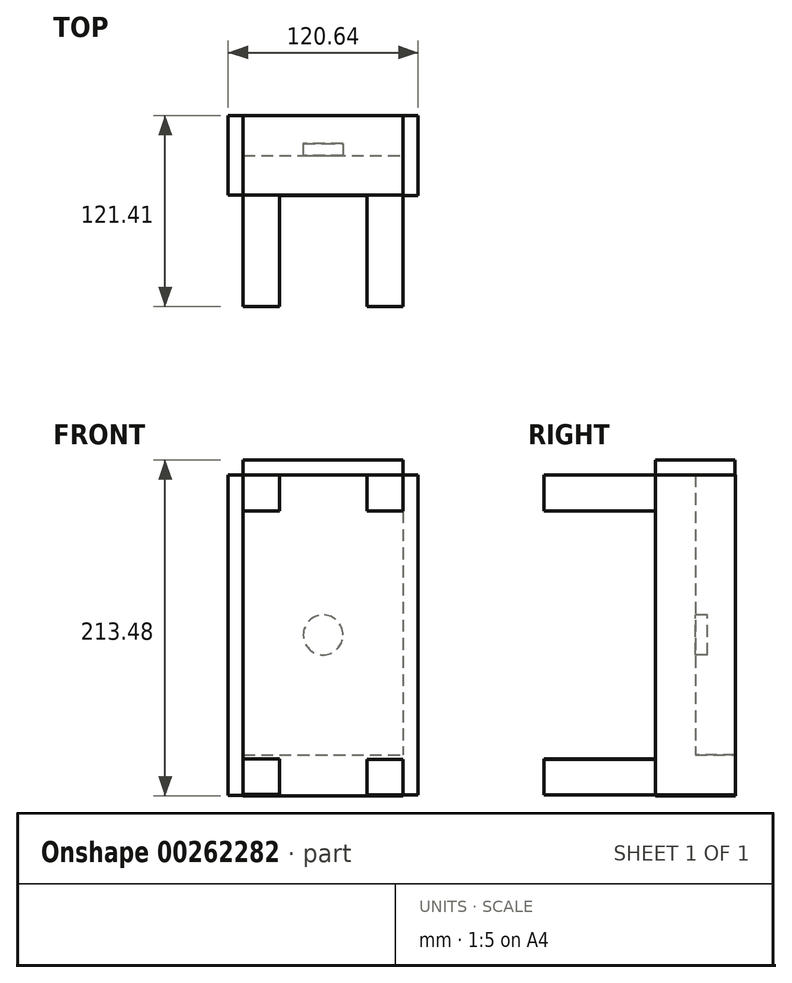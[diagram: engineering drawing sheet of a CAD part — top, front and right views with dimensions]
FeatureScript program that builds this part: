
annotation { "Feature Type Name" : "Feature", "Feature Type Description" : "" }
export const myFeature = defineFeature(function(context is Context, id is Id, definition is map)
    precondition{}
    {
        {
            var Q0;
            Q0=qCreatedBy(makeId("Front.planeOp"),FACE);
            var sketch = newSketch(context, id + "F0", { "sketchPlane" : qUnion([Q0])});
            skLineSegment(sketch, "E0.bottom", {"start": v(-50.8, 101.6) * mm, "end": v(50.8, 101.6) * mm});
            skLineSegment(sketch, "E0.top", {"start": v(-50.8, -101.6) * mm, "end": v(50.8, -101.6) * mm});
            skLineSegment(sketch, "E0.left", {"start": v(-50.8, 101.6) * mm, "end": v(-50.8, -101.6) * mm});
            skLineSegment(sketch, "E0.right", {"start": v(50.8, 101.6) * mm, "end": v(50.8, -101.6) * mm});
            skPoint(sketch, "E0.middle", {"position": v(0, 0) * mm});
            skSolve(sketch);
        }
        {
            var Q0;
            Q0 = qSketchRegion(id + "F0", true);
            extrude(context, id + "F1", {"entities" : qUnion([Q0]), "depth" : 25.4 * mm});
        }
        {
            var Q0;
            Q0=makeQuery(id+"F1.opExtrude","CAP_FACE",FACE,{"disambiguationData":[OSD([sQuery(id+"F0.wireOp",EDGE,"E0.bottom"),sQuery(id+"F0.wireOp",EDGE,"E0.top"),sQuery(id+"F0.wireOp",EDGE,"E0.left"),sQuery(id+"F0.wireOp",EDGE,"E0.right")])],"isStart":false});
            var sketch = newSketch(context, id + "F2", { "sketchPlane" : qUnion([Q0])});
            skPoint(sketch, "E1.middle", {"position": v(0, 54.08) * mm});
            skPoint(sketch, "E2.right.start.orphan", {"position": v(-17.2, 66.12) * mm});
            skPoint(sketch, "E3.bottom.start.orphan", {"position": v(17.2, 66.12) * mm});
            skPoint(sketch, "E3.right.start.orphan", {"position": v(41.3, 66.12) * mm});
            skLineSegment(sketch, "E4.bottom", {"start": v(50.8, 101.6) * mm, "end": v(27.86, 101.6) * mm});
            skLineSegment(sketch, "E4.top", {"start": v(50.8, 78.82) * mm, "end": v(27.86, 78.82) * mm});
            skLineSegment(sketch, "E4.left", {"start": v(50.8, 101.6) * mm, "end": v(50.8, 78.82) * mm});
            skLineSegment(sketch, "E4.right", {"start": v(27.86, 101.6) * mm, "end": v(27.86, 78.82) * mm});
            skPoint(sketch, "E4.middle", {"position": v(39.33, 90.21) * mm});
            skLineSegment(sketch, "E5.left", {"start": v(-35.15, 90.21) * mm, "end": v(-35.15, 90.21) * mm});
            skLineSegment(sketch, "E5.right", {"start": v(113.8, 90.21) * mm, "end": v(113.8, 90.21) * mm});
            skLineSegment(sketch, "E6.bottom", {"start": v(-50.8, 101.6) * mm, "end": v(-27.86, 101.6) * mm});
            skLineSegment(sketch, "E6.left", {"start": v(-50.8, 101.6) * mm, "end": v(-50.8, 78.82) * mm});
            skLineSegment(sketch, "E6.right", {"start": v(-27.86, 101.6) * mm, "end": v(-27.86, 78.82) * mm});
            skPoint(sketch, "E6.middle", {"position": v(-39.33, 90.21) * mm});
            skLineSegment(sketch, "E7.bottom", {"start": v(-39.33, -89.96) * mm, "end": v(-39.33, -89.96) * mm});
            skLineSegment(sketch, "E7.top", {"start": v(-39.33, -94.87) * mm, "end": v(-39.33, -94.87) * mm});
            skLineSegment(sketch, "E7.left", {"start": v(-39.33, -92.41) * mm, "end": v(-39.33, -94.87) * mm});
            skLineSegment(sketch, "E7.right", {"start": v(-39.33, -92.41) * mm, "end": v(-39.33, -94.87) * mm});
            skPoint(sketch, "E7.middle", {"position": v(-39.33, -92.41) * mm});
            skLineSegment(sketch, "E8.bottom", {"start": v(-50.8, -78.64) * mm, "end": v(-27.86, -78.64) * mm});
            skLineSegment(sketch, "E8.top", {"start": v(-50.8, -101.27) * mm, "end": v(-27.86, -101.27) * mm});
            skLineSegment(sketch, "E8.left", {"start": v(-50.8, -78.64) * mm, "end": v(-50.8, -101.27) * mm});
            skLineSegment(sketch, "E8.right", {"start": v(-27.86, -78.64) * mm, "end": v(-27.86, -101.27) * mm});
            skPoint(sketch, "E8.middle", {"position": v(-39.33, -89.96) * mm});
            skLineSegment(sketch, "E9.left", {"start": v(39.33, -92.41) * mm, "end": v(39.33, -92.41) * mm});
            skLineSegment(sketch, "E9.right", {"start": v(-118, -92.41) * mm, "end": v(-118, -92.41) * mm});
            skLineSegment(sketch, "E10.bottom", {"start": v(50.8, -78.89) * mm, "end": v(27.86, -78.89) * mm});
            skLineSegment(sketch, "E10.top", {"start": v(50.8, -101.52) * mm, "end": v(27.86, -101.52) * mm});
            skLineSegment(sketch, "E10.left", {"start": v(50.8, -78.89) * mm, "end": v(50.8, -101.52) * mm});
            skLineSegment(sketch, "E10.right", {"start": v(27.86, -78.89) * mm, "end": v(27.86, -101.52) * mm});
            skPoint(sketch, "E10.middle", {"position": v(39.33, -90.2) * mm});
            skLineSegment(sketch, "E11", {"start": v(-50.8, 78.82) * mm, "end": v(-27.86, 78.82) * mm});
            skSolve(sketch);
        }
        {
            var Q0;
            Q0 = qSketchRegion(id + "F2", true);
            extrude(context, id + "F3", {"entities" : qUnion([Q0]), "operationType" : NewBodyOperationType.ADD, "depth" : 70.61 * mm});
        }
        {
            var Q0;
            Q0=makeQuery(id+"F1.opExtrude","SWEPT_FACE",FACE,{"disambiguationData":[OSD([sQuery(id+"F0.wireOp",EDGE,"E0.right")])]});
            var sketch = newSketch(context, id + "F4", { "sketchPlane" : qUnion([Q0])});
            skLineSegment(sketch, "E12.bottom", {"start": v(-25.4, 101.6) * mm, "end": v(25.4, 101.6) * mm});
            skLineSegment(sketch, "E12.top", {"start": v(-25.4, -101.6) * mm, "end": v(25.4, -101.6) * mm});
            skLineSegment(sketch, "E12.left", {"start": v(-25.4, 101.6) * mm, "end": v(-25.4, -101.6) * mm});
            skLineSegment(sketch, "E12.right", {"start": v(25.4, 101.6) * mm, "end": v(25.4, -101.6) * mm});
            skPoint(sketch, "E12.middle", {"position": v(0, 0) * mm});
            skSolve(sketch);
        }
        {
            var Q0;
            Q0 = qSketchRegion(id + "F4", true);
            extrude(context, id + "F5", {"entities" : qUnion([Q0]), "operationType" : NewBodyOperationType.ADD, "depth" : 9.52 * mm});
        }
        {
            var Q0;
            Q0=makeQuery(id+"F5.boolean.opBoolean","MERGE",FACE,{"derivedFrom":[makeQuery(id+"F1.opExtrude","SWEPT_FACE",FACE,{"disambiguationData":[OSD([sQuery(id+"F0.wireOp",EDGE,"E0.bottom")])]}),makeQuery(id+"F5.opExtrude","SWEPT_FACE",FACE,{"disambiguationData":[OSD([sQuery(id+"F4.wireOp",EDGE,"E12.bottom")])]})]});
            var sketch = newSketch(context, id + "F6", { "sketchPlane" : qUnion([Q0])});
            skLineSegment(sketch, "E13.bottom", {"start": v(-50.83, 25.3) * mm, "end": v(50.83, 25.3) * mm});
            skLineSegment(sketch, "E13.top", {"start": v(-50.83, -25.3) * mm, "end": v(50.83, -25.3) * mm});
            skLineSegment(sketch, "E13.left", {"start": v(-50.83, 25.3) * mm, "end": v(-50.83, -25.3) * mm});
            skLineSegment(sketch, "E13.right", {"start": v(50.83, 25.3) * mm, "end": v(50.83, -25.3) * mm});
            skPoint(sketch, "E13.middle", {"position": v(0, 0) * mm});
            skSolve(sketch);
        }
        {
            var Q0;
            Q0 = qSketchRegion(id + "F6", true);
            extrude(context, id + "F7", {"entities" : qUnion([Q0]), "operationType" : NewBodyOperationType.ADD, "depth" : 9.52 * mm});
        }
        {
            var Q0;
            Q0=makeQuery(id+"F1.opExtrude","SWEPT_FACE",FACE,{"disambiguationData":[OSD([sQuery(id+"F0.wireOp",EDGE,"E0.left")])]});
            var sketch = newSketch(context, id + "F8", { "sketchPlane" : qUnion([Q0])});
            skLineSegment(sketch, "E14.bottom", {"start": v(-25.35, 101.78) * mm, "end": v(25.35, 101.78) * mm});
            skLineSegment(sketch, "E14.top", {"start": v(-25.35, -101.78) * mm, "end": v(25.35, -101.78) * mm});
            skLineSegment(sketch, "E14.left", {"start": v(-25.35, 101.78) * mm, "end": v(-25.35, -101.78) * mm});
            skLineSegment(sketch, "E14.right", {"start": v(25.35, 101.78) * mm, "end": v(25.35, -101.78) * mm});
            skPoint(sketch, "E14.middle", {"position": v(0, 0) * mm});
            skSolve(sketch);
        }
        {
            var Q0;
            Q0 = qSketchRegion(id + "F8", true);
            extrude(context, id + "F9", {"entities" : qUnion([Q0]), "operationType" : NewBodyOperationType.ADD, "depth" : 9.52 * mm});
        }
        {
            var Q0;
            Q0=makeQuery(id+"F5.boolean.opBoolean","MERGE",FACE,{"derivedFrom":[makeQuery(id+"F1.opExtrude","SWEPT_FACE",FACE,{"disambiguationData":[OSD([sQuery(id+"F0.wireOp",EDGE,"E0.top")])]}),makeQuery(id+"F5.opExtrude","SWEPT_FACE",FACE,{"disambiguationData":[OSD([sQuery(id+"F4.wireOp",EDGE,"E12.top")])]})]});
            var sketch = newSketch(context, id + "F10", { "sketchPlane" : qUnion([Q0])});
            skLineSegment(sketch, "E15.bottom", {"start": v(50.8, -25.4) * mm, "end": v(-50.8, -25.4) * mm});
            skLineSegment(sketch, "E15.top", {"start": v(50.8, 25.4) * mm, "end": v(-50.8, 25.4) * mm});
            skLineSegment(sketch, "E15.left", {"start": v(50.8, -25.4) * mm, "end": v(50.8, 25.4) * mm});
            skLineSegment(sketch, "E15.right", {"start": v(-50.8, -25.4) * mm, "end": v(-50.8, 25.4) * mm});
            skPoint(sketch, "E15.middle", {"position": v(0, 0) * mm});
            skSolve(sketch);
        }
        {
            var Q0;
            Q0 = qSketchRegion(id + "F10", true);
            extrude(context, id + "F11", {"entities" : qUnion([Q0]), "operationType" : NewBodyOperationType.ADD, "depth" : 0.76 * mm, "hasSecondDirection" : true, "secondDirectionOppositeDirection" : true, "secondDirectionDepth" : 25.4 * mm});
        }
        {
            var Q0;
            Q0 = qSketchRegion(id + "F2", true);
            extrude(context, id + "F12", {"entities" : qUnion([Q0]), "operationType" : NewBodyOperationType.ADD, "depth" : 25.4 * mm});
        }
        {
            var Q0;
            Q0=makeQuery(id+"F11.boolean.opBoolean","MERGE",FACE,{"derivedFrom":[makeQuery(id+"F5.boolean.opBoolean","MERGE",FACE,{"derivedFrom":[makeQuery(id+"F1.opExtrude","CAP_FACE",FACE,{"disambiguationData":[OSD([sQuery(id+"F0.wireOp",EDGE,"E0.bottom"),sQuery(id+"F0.wireOp",EDGE,"E0.top"),sQuery(id+"F0.wireOp",EDGE,"E0.left"),sQuery(id+"F0.wireOp",EDGE,"E0.right")])],"isStart":false}),makeQuery(id+"F5.opExtrude","SWEPT_FACE",FACE,{"disambiguationData":[OSD([sQuery(id+"F4.wireOp",EDGE,"E12.left")])]})]}),makeQuery(id+"F11.opExtrude","SWEPT_FACE",FACE,{"disambiguationData":[OSD([sQuery(id+"F10.wireOp",EDGE,"E15.top")])]})]});
            var sketch = newSketch(context, id + "F13", { "sketchPlane" : qUnion([Q0])});
            skCircle(sketch, "E16", {"center": v(0, 0) * mm, "radius": 12.66 * mm});
            skSolve(sketch);
        }
        {
            var Q0;
            Q0 = qSketchRegion(id + "F13", true);
            extrude(context, id + "F14", {"entities" : qUnion([Q0]), "operationType" : NewBodyOperationType.ADD, "oppositeDirection" : true, "depth" : 33.02 * mm});
        }
    });
